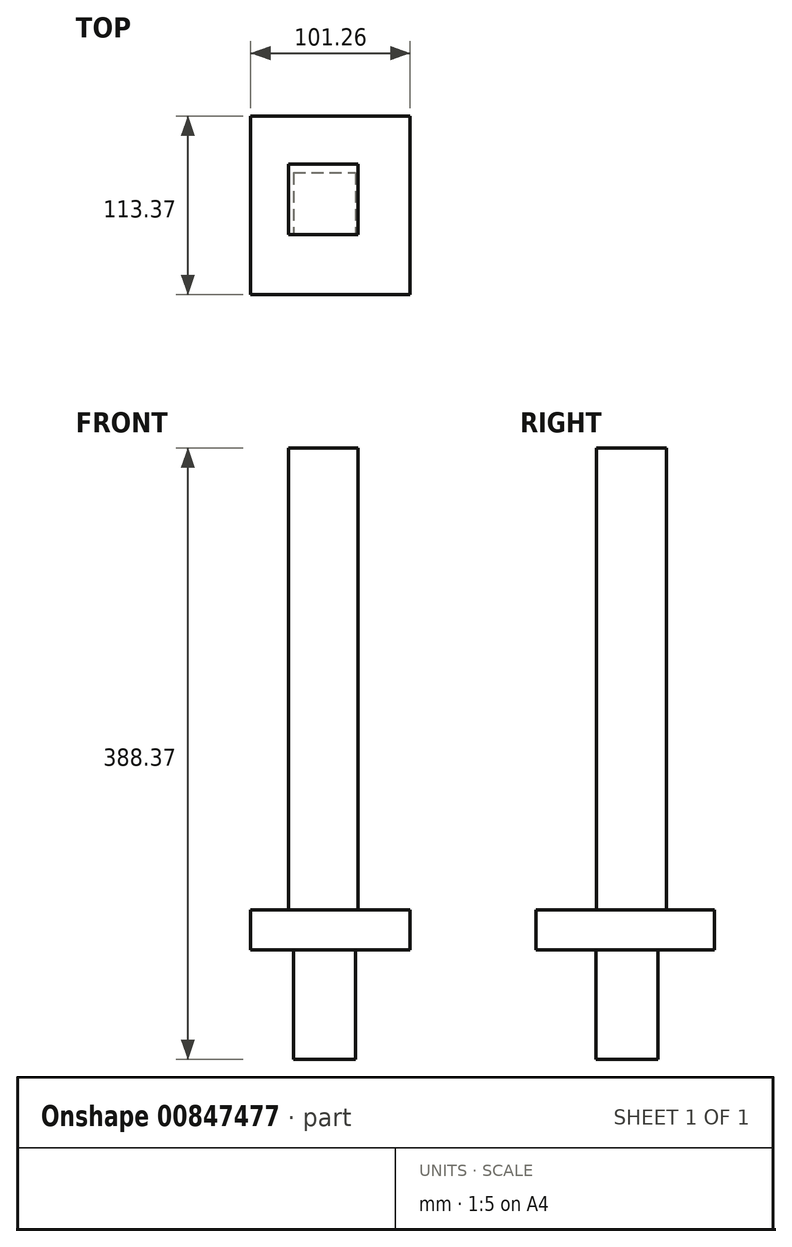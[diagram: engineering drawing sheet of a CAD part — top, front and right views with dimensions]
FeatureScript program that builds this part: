
annotation { "Feature Type Name" : "Feature", "Feature Type Description" : "" }
export const myFeature = defineFeature(function(context is Context, id is Id, definition is map)
    precondition{}
    {
        {
            var Q0;
            Q0=qCreatedBy(makeId("Top.planeOp"),FACE);
            var sketch = newSketch(context, id + "F0", { "sketchPlane" : qUnion([Q0])});
            skLineSegment(sketch, "E0.bottom", {"start": v(-125.63, -27.21) * mm, "end": v(-86.23, -27.21) * mm});
            skLineSegment(sketch, "E0.top", {"start": v(-125.63, -66.52) * mm, "end": v(-86.23, -66.52) * mm});
            skLineSegment(sketch, "E0.left", {"start": v(-125.63, -27.21) * mm, "end": v(-125.63, -66.52) * mm});
            skLineSegment(sketch, "E0.right", {"start": v(-86.23, -27.21) * mm, "end": v(-86.23, -66.52) * mm});
            skSolve(sketch);
        }
        {
            var Q0;
            Q0=makeQuery(id+"F0.imprint","IMPRINT",FACE,{"disambiguationData":[TD([[makeQuery(id+"F0.imprint","IMPRINT",EDGE,{"derivedFrom":sQuery(id+"F0.wireOp",EDGE,"E0.bottom")}),-1.0]])]});
            extrude(context, id + "F1", {"entities" : qUnion([Q0]), "depth" : 34.8 * mm, "offsetDistance" : 25.4 * mm});
        }
        {
            var Q0;
            Q0=makeQuery(id+"F1.opExtrude","CAP_FACE",FACE,{"disambiguationData":[OSD([sQuery(id+"F0.wireOp",EDGE,"E0.bottom"),sQuery(id+"F0.wireOp",EDGE,"E0.top"),sQuery(id+"F0.wireOp",EDGE,"E0.left"),sQuery(id+"F0.wireOp",EDGE,"E0.right")])],"isStart":false});
            var sketch = newSketch(context, id + "F2", { "sketchPlane" : qUnion([Q0])});
            skLineSegment(sketch, "E1.bottom", {"start": v(-125.63, -27.21) * mm, "end": v(-86.23, -27.21) * mm});
            skLineSegment(sketch, "E1.top", {"start": v(-125.63, -66.52) * mm, "end": v(-86.23, -66.52) * mm});
            skLineSegment(sketch, "E1.left", {"start": v(-125.63, -27.21) * mm, "end": v(-125.63, -66.52) * mm});
            skLineSegment(sketch, "E1.right", {"start": v(-86.23, -27.21) * mm, "end": v(-86.23, -66.52) * mm});
            skSolve(sketch);
        }
        {
            var Q0;
            Q0 = qSketchRegion(id + "F2", true);
            extrude(context, id + "F3", {"entities" : qUnion([Q0]), "operationType" : NewBodyOperationType.ADD, "depth" : 34.8 * mm, "offsetDistance" : 25.4 * mm});
        }
        {
            var Q0;
            Q0=makeQuery(id+"F3.opExtrude","CAP_FACE",FACE,{"disambiguationData":[OSD([sQuery(id+"F2.wireOp",EDGE,"E1.bottom"),sQuery(id+"F2.wireOp",EDGE,"E1.top"),sQuery(id+"F2.wireOp",EDGE,"E1.left"),sQuery(id+"F2.wireOp",EDGE,"E1.right")])],"isStart":false});
            var sketch = newSketch(context, id + "F4", { "sketchPlane" : qUnion([Q0])});
            skLineSegment(sketch, "E2.bottom", {"start": v(-152.8, 8.83) * mm, "end": v(-51.54, 8.83) * mm});
            skLineSegment(sketch, "E2.top", {"start": v(-152.8, -104.54) * mm, "end": v(-51.54, -104.54) * mm});
            skLineSegment(sketch, "E2.left", {"start": v(-152.8, 8.83) * mm, "end": v(-152.8, -104.54) * mm});
            skLineSegment(sketch, "E2.right", {"start": v(-51.54, 8.83) * mm, "end": v(-51.54, -104.54) * mm});
            skSolve(sketch);
        }
        {
            var Q0;
            Q0 = qSketchRegion(id + "F4", true);
            extrude(context, id + "F5", {"entities" : qUnion([Q0]), "operationType" : NewBodyOperationType.ADD, "depth" : 25.4 * mm, "offsetDistance" : 25.4 * mm});
        }
        {
            var Q0;
            Q0=makeQuery(id+"F5.opExtrude","CAP_FACE",FACE,{"disambiguationData":[OSD([sQuery(id+"F4.wireOp",EDGE,"E2.bottom"),sQuery(id+"F4.wireOp",EDGE,"E2.top"),sQuery(id+"F4.wireOp",EDGE,"E2.left"),sQuery(id+"F4.wireOp",EDGE,"E2.right")])],"isStart":false});
            var sketch = newSketch(context, id + "F6", { "sketchPlane" : qUnion([Q0])});
            skLineSegment(sketch, "E3.bottom", {"start": v(-128.79, -21.74) * mm, "end": v(-84.75, -21.74) * mm});
            skLineSegment(sketch, "E3.top", {"start": v(-128.79, -66.32) * mm, "end": v(-84.75, -66.32) * mm});
            skLineSegment(sketch, "E3.left", {"start": v(-128.79, -21.74) * mm, "end": v(-128.79, -66.32) * mm});
            skLineSegment(sketch, "E3.right", {"start": v(-84.75, -21.74) * mm, "end": v(-84.75, -66.32) * mm});
            skSolve(sketch);
        }
        {
            var Q0;
            Q0 = qSketchRegion(id + "F6", true);
            extrude(context, id + "F7", {"entities" : qUnion([Q0]), "operationType" : NewBodyOperationType.ADD, "depth" : 293.37 * mm, "offsetDistance" : 25.4 * mm});
        }
    });
